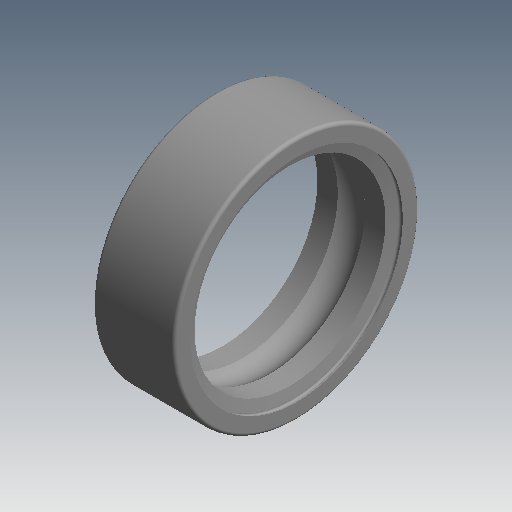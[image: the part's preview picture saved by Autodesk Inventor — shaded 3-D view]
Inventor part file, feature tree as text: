
AUTODESK INVENTOR PART (.ipt)
format: ipt  version: 2020 (Build 240168000, 168)  size: 167,424 bytes
history: native  units: mm (DEFAULTED — no unit token found)
features: revolve x1, sketch x1
ambient origin geometry x8: Origin, YZ Plane, XZ Plane, XY Plane, X Axis, Y Axis, Z Axis, Center Point
bodies: Solid1 (feature_tree)
feature tree (2):
  revolve  "Revolution1"  [1 undecoded]
  sketch  "Sketch_17"  dims[d0=360.0deg]
note: 1 required parameter value undecoded (feature->parameter linkage not recoverable at this tier; creation-order binding heuristic only, values carry confidence <= 0.55)
